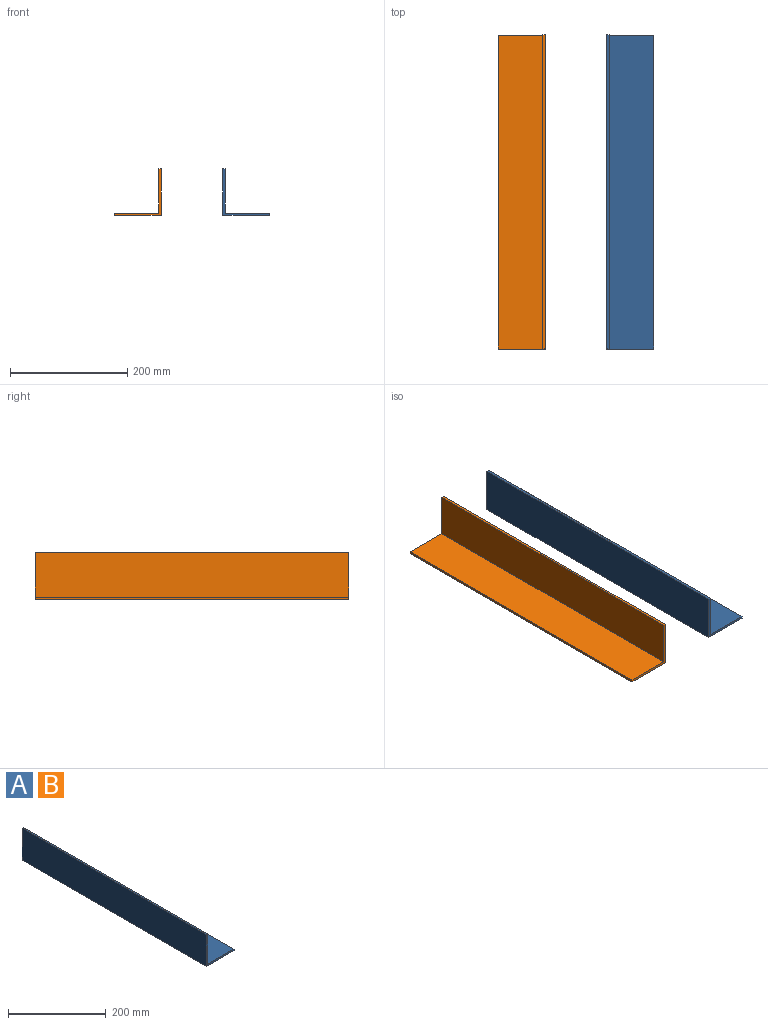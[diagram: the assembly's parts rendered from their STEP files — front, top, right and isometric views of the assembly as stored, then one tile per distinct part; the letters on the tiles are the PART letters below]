
ASSEMBLY  parts=2 mates=1
PART A: 8 faces, bbox 80x534.5x80 mm
  f0: plane 80x80mm, normal (0,-1,0), area 624mm2, adj f2,f3,f4,f5,f6,f7
  f1: plane 80x80mm, normal (0,1,0), area 624mm2, adj f2,f3,f4,f5,f6,f7
  f2: plane 534.53x4mm, normal (0,0,1), area 2138.1mm2, adj f0,f1,f4,f6
  f3: plane 534.53x4mm, normal (1,0,0), area 2138.1mm2, adj f0,f1,f5,f7
  f4: plane 534.53x80mm, normal (-1,0,0), area 42762.5mm2, adj f0,f1,f2,f5
  f5: plane 534.53x80mm, normal (0,0,-1), area 42762.5mm2, adj f0,f1,f3,f4
  f6: plane 534.53x76mm, normal (1,0,0), area 40624.4mm2, adj f0,f1,f2,f7
  f7: plane 534.53x76mm, normal (0,0,1), area 40624.4mm2, adj f0,f1,f3,f6
PART B: same geometry as A
PLACE A at identity fixed
PLACE B rot(axis=(0,0,1),180deg) t=(-104.89,0,0)mm
MATE slider A.f4 <-> B.f4  axis (-1,0,0) through (0,0,40)mm
